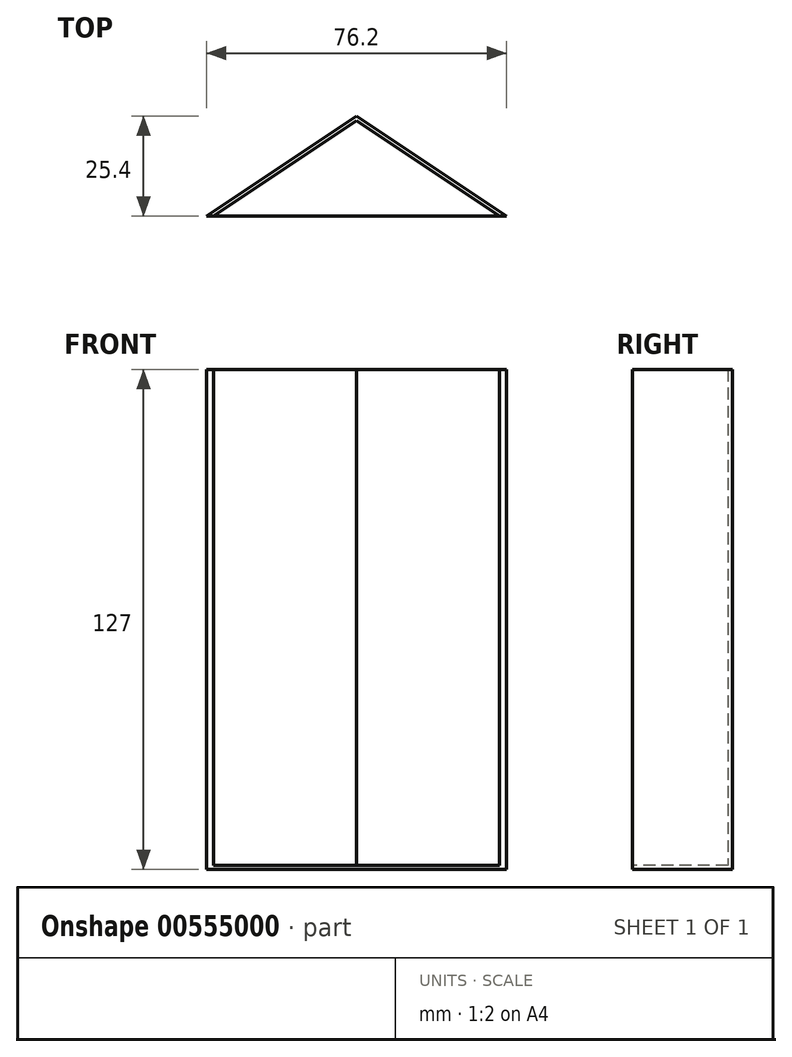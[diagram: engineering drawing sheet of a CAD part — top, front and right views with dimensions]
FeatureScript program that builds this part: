
annotation { "Feature Type Name" : "Feature", "Feature Type Description" : "" }
export const myFeature = defineFeature(function(context is Context, id is Id, definition is map)
    precondition{}
    {
        {
            var Q0;
            Q0=qCreatedBy(makeId("Top.planeOp"),FACE);
            var sketch = newSketch(context, id + "F0", { "sketchPlane" : qUnion([Q0])});
            skLineSegment(sketch, "E0.bottom", {"start": v(38.1, 12.7) * mm, "end": v(-38.1, 12.7) * mm});
            skLineSegment(sketch, "E0.top", {"start": v(38.1, -12.7) * mm, "end": v(-38.1, -12.7) * mm});
            skLineSegment(sketch, "E0.left", {"start": v(38.1, 12.7) * mm, "end": v(38.1, -12.7) * mm});
            skLineSegment(sketch, "E0.right", {"start": v(-38.1, 12.7) * mm, "end": v(-38.1, -12.7) * mm});
            skPoint(sketch, "E0.middle", {"position": v(0, 0) * mm});
            skLineSegment(sketch, "E1", {"start": v(-38.1, -12.7) * mm, "end": v(0, 12.7) * mm});
            skLineSegment(sketch, "E2", {"start": v(0, 12.7) * mm, "end": v(38.1, -12.7) * mm});
            skSolve(sketch);
        }
        {
            var Q0;
            Q0=makeQuery(id+"F0.imprint","IMPRINT",FACE,{"disambiguationData":[TD([[makeQuery(id+"F0.imprint","IMPRINT",EDGE,{"derivedFrom":sQuery(id+"F0.wireOp",EDGE,"E0.top")}),-1.0]])]});
            extrude(context, id + "F1", {"entities" : qUnion([Q0]), "depth" : 127 * mm, "offsetDistance" : 25.4 * mm});
        }
        {
            var Q0;
            Q0=makeQuery(id+"F1.opExtrude","CAP_FACE",FACE,{"disambiguationData":[OSD([sQuery(id+"F0.wireOp",EDGE,"E0.top"),sQuery(id+"F0.wireOp",EDGE,"E1"),sQuery(id+"F0.wireOp",EDGE,"E2")])],"isStart":false});
            var Q1;
            Q1=makeQuery(id+"F1.opExtrude","SWEPT_FACE",FACE,{"disambiguationData":[OSD([sQuery(id+"F0.wireOp",EDGE,"E0.top")])]});
            shell(context, id + "F2", {"entities" : qUnion([Q0, Q1]), "thickness" : 1 * mm});
        }
    });
